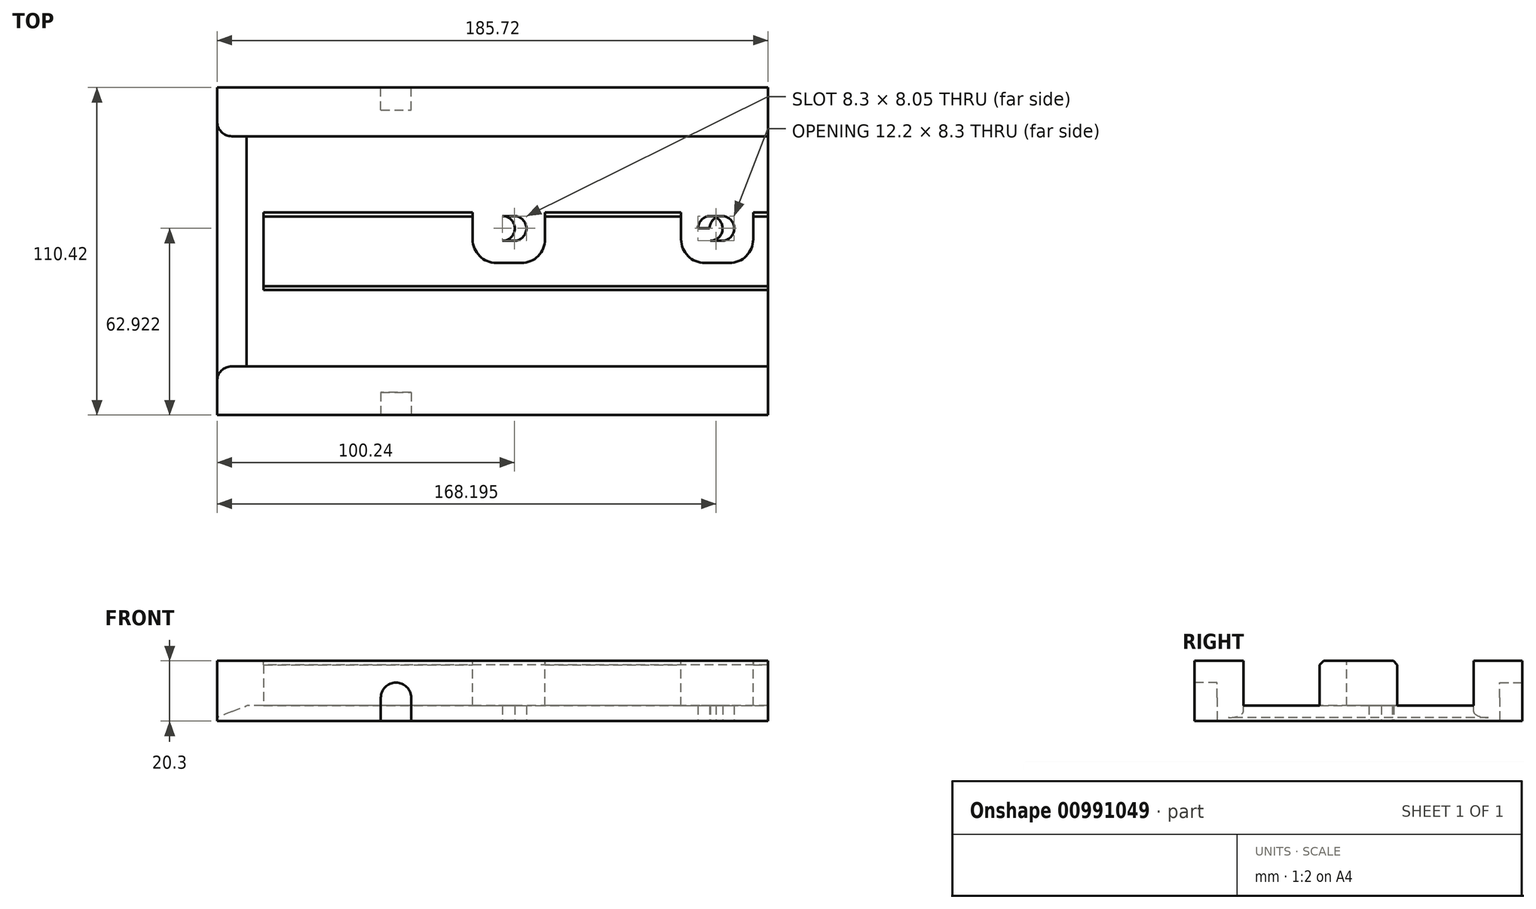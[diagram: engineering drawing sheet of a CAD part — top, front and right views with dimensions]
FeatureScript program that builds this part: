
annotation { "Feature Type Name" : "Feature", "Feature Type Description" : "" }
export const myFeature = defineFeature(function(context is Context, id is Id, definition is map)
    precondition{}
    {
        {
            var Q0;
            Q0=qCreatedBy(makeId("Top.planeOp"),FACE);
            var sketch = newSketch(context, id + "F0", { "sketchPlane" : qUnion([Q0])});
            skLineSegment(sketch, "E0.bottom", {"start": v(-101.07, 45.3) * mm, "end": v(84.65, 45.3) * mm});
            skLineSegment(sketch, "E0.top", {"start": v(-101.07, -65.12) * mm, "end": v(84.65, -65.12) * mm});
            skLineSegment(sketch, "E0.left", {"start": v(-101.07, 45.3) * mm, "end": v(-101.07, -65.12) * mm});
            skLineSegment(sketch, "E0.right", {"start": v(84.65, 45.3) * mm, "end": v(84.65, -65.12) * mm});
            skSolve(sketch);
        }
        {
            var Q0;
            Q0 = qSketchRegion(id + "F0", true);
            extrude(context, id + "F1", {"entities" : qUnion([Q0]), "depth" : 5.2 * mm, "offsetDistance" : 25 * mm});
        }
        {
            var Q0;
            Q0=makeQuery(id+"F1.opExtrude","SWEPT_FACE",FACE,{"disambiguationData":[OSD([sQuery(id+"F0.wireOp",EDGE,"E0.top")])]});
            var sketch = newSketch(context, id + "F2", { "sketchPlane" : qUnion([Q0])});
            skLineSegment(sketch, "E1", {"start": v(-101.07, 5.2) * mm, "end": v(-91.07, 5.2) * mm});
            skLineSegment(sketch, "E2", {"start": v(-101.07, 1.2) * mm, "end": v(-91.07, 5.2) * mm});
            skLineSegment(sketch, "E3", {"start": v(-101.07, 1.2) * mm, "end": v(-101.07, 5.2) * mm});
            skLineSegment(sketch, "E4", {"start": v(-91.07, 5.2) * mm, "end": v(-101.07, 1.2) * mm});
            skSolve(sketch);
        }
        {
            var Q0;
            Q0=makeQuery(id+"F2.imprint","IMPRINT",FACE,{"disambiguationData":[TD([[makeQuery(id+"F2.imprint","IMPRINT",EDGE,{"derivedFrom":sQuery(id+"F2.wireOp",EDGE,"E1")}),-1.0]])]});
            extrude(context, id + "F3", {"entities" : qUnion([Q0]), "operationType" : NewBodyOperationType.REMOVE, "endBound" : BoundingType.UP_TO_NEXT, "oppositeDirection" : true, "depth" : 25 * mm, "offsetDistance" : 25 * mm});
        }
        {
            var Q0;
            Q0=makeQuery(id+"F1.opExtrude","CAP_FACE",FACE,{"disambiguationData":[OSD([sQuery(id+"F0.wireOp",EDGE,"E0.bottom"),sQuery(id+"F0.wireOp",EDGE,"E0.top"),sQuery(id+"F0.wireOp",EDGE,"E0.left"),sQuery(id+"F0.wireOp",EDGE,"E0.right")])],"isStart":true});
            var sketch = newSketch(context, id + "F4", { "sketchPlane" : qUnion([Q0])});
            skLineSegment(sketch, "E5.bottom", {"start": v(-101.07, 65.12) * mm, "end": v(84.65, 65.12) * mm});
            skLineSegment(sketch, "E5.top", {"start": v(-101.07, 48.72) * mm, "end": v(84.65, 48.72) * mm});
            skLineSegment(sketch, "E5.left", {"start": v(-101.07, 65.12) * mm, "end": v(-101.07, 48.72) * mm});
            skLineSegment(sketch, "E5.right", {"start": v(84.65, 65.12) * mm, "end": v(84.65, 48.72) * mm});
            skLineSegment(sketch, "E6.bottom", {"start": v(-101.07, -45.3) * mm, "end": v(84.65, -45.3) * mm});
            skLineSegment(sketch, "E6.top", {"start": v(-101.07, -28.9) * mm, "end": v(84.65, -28.9) * mm});
            skLineSegment(sketch, "E6.left", {"start": v(-101.07, -45.3) * mm, "end": v(-101.07, -28.9) * mm});
            skLineSegment(sketch, "E6.right", {"start": v(84.65, -45.3) * mm, "end": v(84.65, -28.9) * mm});
            skLineSegment(sketch, "E7.top", {"start": v(84.65, 22.96) * mm, "end": v(-85.35, 22.96) * mm});
            skLineSegment(sketch, "E7.left", {"start": v(84.65, 9.9) * mm, "end": v(84.65, 22.96) * mm});
            skLineSegment(sketch, "E7.right", {"start": v(-85.35, 9.9) * mm, "end": v(-85.35, 22.96) * mm});
            skLineSegment(sketch, "E8.top", {"start": v(-85.35, -3.14) * mm, "end": v(84.65, -3.14) * mm});
            skLineSegment(sketch, "E8.left", {"start": v(-85.35, 9.9) * mm, "end": v(-85.35, -3.14) * mm});
            skLineSegment(sketch, "E8.right", {"start": v(84.65, 9.9) * mm, "end": v(84.65, -3.14) * mm});
            skPoint(sketch, "E9.start.orphan", {"position": v(-101.07, 9.9) * mm});
            skSolve(sketch);
        }
        {
            var Q0;
            Q0 = qSketchRegion(id + "F4", true);
            extrude(context, id + "F5", {"entities" : qUnion([Q0]), "operationType" : NewBodyOperationType.ADD, "oppositeDirection" : true, "depth" : 20.3 * mm, "offsetDistance" : 25 * mm});
        }
        {
            var Q0;
            Q0=makeQuery(id+"F5.opExtrude","CAP_FACE",FACE,{"disambiguationData":[OSD([sQuery(id+"F4.wireOp",EDGE,"E7.top"),sQuery(id+"F4.wireOp",EDGE,"E7.left"),sQuery(id+"F4.wireOp",EDGE,"E7.right"),sQuery(id+"F4.wireOp",EDGE,"E8.top"),sQuery(id+"F4.wireOp",EDGE,"E8.left"),sQuery(id+"F4.wireOp",EDGE,"E8.right")])],"isStart":false});
            var sketch = newSketch(context, id + "F6", { "sketchPlane" : qUnion([Q0])});
            skLineSegment(sketch, "E10", {"start": v(84.65, 3.14) * mm, "end": v(79.65, 3.14) * mm});
            skLineSegment(sketch, "E11.bottom", {"start": v(79.65, 3.14) * mm, "end": v(55.35, 3.14) * mm});
            skLineSegment(sketch, "E11.top", {"start": v(79.65, -13.86) * mm, "end": v(55.35, -13.86) * mm});
            skLineSegment(sketch, "E11.left", {"start": v(79.65, 3.14) * mm, "end": v(79.65, -13.86) * mm});
            skLineSegment(sketch, "E11.right", {"start": v(55.35, 3.14) * mm, "end": v(55.35, -13.86) * mm});
            skLineSegment(sketch, "E12", {"start": v(84.65, 3.14) * mm, "end": v(9.49, 3.14) * mm});
            skLineSegment(sketch, "E13.bottom", {"start": v(9.49, 3.14) * mm, "end": v(-14.91, 3.14) * mm});
            skLineSegment(sketch, "E13.top", {"start": v(9.49, -13.86) * mm, "end": v(-14.91, -13.86) * mm});
            skLineSegment(sketch, "E13.left", {"start": v(9.49, 3.14) * mm, "end": v(9.49, -13.86) * mm});
            skLineSegment(sketch, "E13.right", {"start": v(-14.91, 3.14) * mm, "end": v(-14.91, -13.86) * mm});
            skSolve(sketch);
        }
        {
            var Q0;
            Q0=makeQuery(id+"F6.imprint","IMPRINT",FACE,{"disambiguationData":[TD([[makeQuery(id+"F6.imprint","IMPRINT",EDGE,{"derivedFrom":sQuery(id+"F6.wireOp",EDGE,"E13.bottom")}),-1.0]])]});
            var Q1;
            Q1=makeQuery(id+"F6.imprint","IMPRINT",FACE,{"disambiguationData":[TD([[makeQuery(id+"F6.imprint","IMPRINT",EDGE,{"derivedFrom":sQuery(id+"F6.wireOp",EDGE,"E11.bottom")}),-1.0]])]});
            extrude(context, id + "F7", {"entities" : qUnion([Q0, Q1]), "operationType" : NewBodyOperationType.REMOVE, "oppositeDirection" : true, "depth" : 15.1 * mm, "offsetDistance" : 25 * mm});
        }
        {
            var Q0;
            Q0=makeQuery(id+"F7.boolean.opBoolean","COPY",EDGE,{"derivedFrom":makeQuery(id+"F7.opExtrude","SWEPT_EDGE",EDGE,{"disambiguationData":[OSD([sQuery(id+"F6.wireOp",EDGE,"E13.top"),sQuery(id+"F6.wireOp",EDGE,"E13.right")])]})});
            fillet(context, id + "F8", {"entities" : qUnion([Q0]), "radius" : 8 * mm, "tangentPropagation" : true, "allowEdgeOverflow" : false});
        }
        {
            var Q0;
            Q0=makeQuery(id+"F7.boolean.opBoolean","COPY",EDGE,{"derivedFrom":makeQuery(id+"F7.opExtrude","SWEPT_EDGE",EDGE,{"disambiguationData":[OSD([sQuery(id+"F6.wireOp",EDGE,"E13.top"),sQuery(id+"F6.wireOp",EDGE,"E13.left")])]})});
            var Q1;
            Q1=makeQuery(id+"F7.boolean.opBoolean","COPY",EDGE,{"derivedFrom":makeQuery(id+"F7.opExtrude","SWEPT_EDGE",EDGE,{"disambiguationData":[OSD([sQuery(id+"F6.wireOp",EDGE,"E11.top"),sQuery(id+"F6.wireOp",EDGE,"E11.left")])]})});
            var Q2;
            Q2=makeQuery(id+"F7.boolean.opBoolean","COPY",EDGE,{"derivedFrom":makeQuery(id+"F7.opExtrude","SWEPT_EDGE",EDGE,{"disambiguationData":[OSD([sQuery(id+"F6.wireOp",EDGE,"E11.top"),sQuery(id+"F6.wireOp",EDGE,"E11.right")])]})});
            fillet(context, id + "F9", {"entities" : qUnion([Q0, Q1, Q2]), "radius" : 8 * mm, "tangentPropagation" : true, "allowEdgeOverflow" : false});
        }
        {
            var Q0;
            Q0=makeQuery(id+"F5.opExtrude","SWEPT_EDGE",EDGE,{"disambiguationData":[OSD([sQuery(id+"F0.wireOp",EDGE,"E0.left"),sQuery(id+"F4.wireOp",EDGE,"E6.top"),sQuery(id+"F4.wireOp",EDGE,"E6.left")])]});
            var Q1;
            Q1=makeQuery(id+"F5.opExtrude","SWEPT_EDGE",EDGE,{"disambiguationData":[OSD([sQuery(id+"F0.wireOp",EDGE,"E0.left"),sQuery(id+"F4.wireOp",EDGE,"E5.top"),sQuery(id+"F4.wireOp",EDGE,"E5.left")])]});
            fillet(context, id + "F10", {"entities" : qUnion([Q0, Q1]), "radius" : 5 * mm, "tangentPropagation" : true, "allowEdgeOverflow" : false});
        }
        {
            var Q0;
            {var subQ1=sQuery(id+"F4.wireOp",EDGE,"E8.top");Q0=makeQuery(id+"F7.boolean.opBoolean","SPLIT",EDGE,{"disambiguationData":[TD([makeQuery(id+"F7.opExtrude","SWEPT_FACE",FACE,{"disambiguationData":[OSD([sQuery(id+"F6.wireOp",EDGE,"E13.right")])]})])],"derivedFrom":makeQuery(id+"F5.opExtrude","CAP_EDGE",EDGE,{"disambiguationData":[OSD([subQ1])],"isStart":false})});}
            var Q1;
            {var subQ0=sQuery(id+"F4.wireOp",EDGE,"E8.top");Q1=makeQuery(id+"F7.boolean.opBoolean","SPLIT",EDGE,{"disambiguationData":[TD([makeQuery(id+"F7.opExtrude","SWEPT_FACE",FACE,{"disambiguationData":[OSD([sQuery(id+"F6.wireOp",EDGE,"E11.right")])]})])],"derivedFrom":makeQuery(id+"F5.opExtrude","CAP_EDGE",EDGE,{"disambiguationData":[OSD([subQ0])],"isStart":false})});}
            var Q2;
            {var subQ1=sQuery(id+"F4.wireOp",EDGE,"E8.top");Q2=makeQuery(id+"F7.boolean.opBoolean","SPLIT",EDGE,{"disambiguationData":[TD([makeQuery(id+"F1.opExtrude","SWEPT_FACE",FACE,{"disambiguationData":[OSD([sQuery(id+"F0.wireOp",EDGE,"E0.right")])]})])],"derivedFrom":makeQuery(id+"F5.opExtrude","CAP_EDGE",EDGE,{"disambiguationData":[OSD([subQ1])],"isStart":false})});}
            var Q3;
            Q3=makeQuery(id+"F5.opExtrude","CAP_EDGE",EDGE,{"disambiguationData":[OSD([sQuery(id+"F4.wireOp",EDGE,"E7.top")])],"isStart":false});
            chamfer(context, id + "F11", {"entities" : qUnion([Q0, Q1, Q2, Q3]), "width" : 1.3 * mm, "tangentPropagation" : true});
        }
        {
            var Q0;
            Q0=makeQuery(id+"F1.opExtrude","CAP_FACE",FACE,{"disambiguationData":[OSD([sQuery(id+"F0.wireOp",EDGE,"E0.bottom"),sQuery(id+"F0.wireOp",EDGE,"E0.top"),sQuery(id+"F0.wireOp",EDGE,"E0.left"),sQuery(id+"F0.wireOp",EDGE,"E0.right")])],"isStart":true});
            var sketch = newSketch(context, id + "F12", { "sketchPlane" : qUnion([Q0])});
            skLineSegment(sketch, "E14", {"start": v(-101.07, 65.12) * mm, "end": v(-101.07, -45.3) * mm});
            skLineSegment(sketch, "E15", {"start": v(84.65, -45.3) * mm, "end": v(84.65, 2.2) * mm});
            skLineSegment(sketch, "E16", {"start": v(84.65, 2.2) * mm, "end": v(69.08, 2.2) * mm});
            skCircle(sketch, "E17", {"center": v(69.08, 2.2) * mm, "radius": 4.15 * mm});
            skLineSegment(sketch, "E18", {"start": v(69.08, 2.2) * mm, "end": v(65.18, 2.2) * mm});
            skCircle(sketch, "E19", {"center": v(65.18, 2.2) * mm, "radius": 4.15 * mm});
            skLineSegment(sketch, "E20", {"start": v(65.18, 6.35) * mm, "end": v(69.08, 6.35) * mm});
            skLineSegment(sketch, "E21", {"start": v(65.18, -1.95) * mm, "end": v(69.08, -1.95) * mm});
            skLineSegment(sketch, "E22", {"start": v(84.65, 2.2) * mm, "end": v(-0.95, 2.2) * mm});
            skLineSegment(sketch, "E23", {"start": v(-0.95, 2.2) * mm, "end": v(-4.85, 2.2) * mm});
            skCircle(sketch, "E24", {"center": v(-0.95, 2.2) * mm, "radius": 4.15 * mm});
            skCircle(sketch, "E25", {"center": v(-4.85, 2.2) * mm, "radius": 4.15 * mm});
            skLineSegment(sketch, "E26", {"start": v(-4.85, 6.35) * mm, "end": v(-0.95, 6.35) * mm});
            skLineSegment(sketch, "E27", {"start": v(-4.85, -1.95) * mm, "end": v(-0.95, -1.95) * mm});
            skPoint(sketch, "E28", {"position": v(3.2, 2.2) * mm});
            skSolve(sketch);
        }
        {
            var Q0;
            Q0=makeQuery(id+"F5.boolean.opBoolean","MERGE",FACE,{"derivedFrom":[makeQuery(id+"F1.opExtrude","SWEPT_FACE",FACE,{"disambiguationData":[OSD([sQuery(id+"F0.wireOp",EDGE,"E0.top")])]}),makeQuery(id+"F5.opExtrude","SWEPT_FACE",FACE,{"disambiguationData":[OSD([sQuery(id+"F4.wireOp",EDGE,"E5.bottom")])]})]});
            var sketch = newSketch(context, id + "F13", { "sketchPlane" : qUnion([Q0])});
            skLineSegment(sketch, "E29", {"start": v(-101.07, 0) * mm, "end": v(-40.77, 0) * mm});
            skLineSegment(sketch, "E30", {"start": v(-40.77, 0) * mm, "end": v(-40.77, 7.91) * mm});
            skCircle(sketch, "E31", {"center": v(-40.77, 7.91) * mm, "radius": 5.1 * mm});
            skLineSegment(sketch, "E32", {"start": v(-45.87, 7.91) * mm, "end": v(-35.67, 7.91) * mm});
            skLineSegment(sketch, "E33.top", {"start": v(-45.87, 0) * mm, "end": v(-35.67, 0) * mm});
            skLineSegment(sketch, "E33.left", {"start": v(-45.87, 7.91) * mm, "end": v(-45.87, 0) * mm});
            skLineSegment(sketch, "E33.right", {"start": v(-35.67, 7.91) * mm, "end": v(-35.67, 0) * mm});
            skSolve(sketch);
        }
        {
            var Q0;
            Q0 = qSketchRegion(id + "F13", true);
            extrude(context, id + "F14", {"entities" : qUnion([Q0]), "operationType" : NewBodyOperationType.REMOVE, "oppositeDirection" : true, "depth" : 7.6 * mm, "offsetDistance" : 25 * mm});
        }
        {
            var Q0;
            Q0=makeQuery(id+"F5.boolean.opBoolean","MERGE",FACE,{"derivedFrom":[makeQuery(id+"F1.opExtrude","SWEPT_FACE",FACE,{"disambiguationData":[OSD([sQuery(id+"F0.wireOp",EDGE,"E0.bottom")])]}),makeQuery(id+"F5.opExtrude","SWEPT_FACE",FACE,{"disambiguationData":[OSD([sQuery(id+"F4.wireOp",EDGE,"E6.bottom")])]})]});
            var sketch = newSketch(context, id + "F15", { "sketchPlane" : qUnion([Q0])});
            skLineSegment(sketch, "E34.bottom", {"start": v(101.07, 0) * mm, "end": v(40.77, 0) * mm});
            skLineSegment(sketch, "E34.top", {"start": v(101.07, 7.9) * mm, "end": v(40.77, 7.9) * mm});
            skLineSegment(sketch, "E34.left", {"start": v(101.07, 0) * mm, "end": v(101.07, 7.9) * mm});
            skLineSegment(sketch, "E34.right", {"start": v(40.77, 0) * mm, "end": v(40.77, 7.9) * mm});
            skCircle(sketch, "E35", {"center": v(40.77, 7.9) * mm, "radius": 5.1 * mm});
            skLineSegment(sketch, "E36", {"start": v(45.87, 7.9) * mm, "end": v(35.67, 7.9) * mm});
            skLineSegment(sketch, "E37.bottom", {"start": v(35.67, 7.9) * mm, "end": v(45.87, 7.9) * mm});
            skLineSegment(sketch, "E37.top", {"start": v(35.67, 0) * mm, "end": v(45.87, 0) * mm});
            skLineSegment(sketch, "E37.left", {"start": v(35.67, 7.9) * mm, "end": v(35.67, 0) * mm});
            skLineSegment(sketch, "E37.right", {"start": v(45.87, 7.9) * mm, "end": v(45.87, 0) * mm});
            skSolve(sketch);
        }
        {
            var Q0;
            {var subQ3=sQuery(id+"F15.wireOp",EDGE,"E37.right");Q0=makeQuery(id+"F15.imprint","IMPRINT",FACE,{"disambiguationData":[TD([[makeQuery(id+"F15.imprint","IMPRINT",EDGE,{"derivedFrom":subQ3}),-1.0]])]});}
            var Q1;
            {var subQ0=sQuery(id+"F15.wireOp",EDGE,"E37.top");Q1=makeQuery(id+"F15.imprint","IMPRINT",FACE,{"disambiguationData":[TD([[makeQuery(id+"F15.imprint","IMPRINT",EDGE,{"derivedFrom":subQ0}),-1.0]])]});}
            var Q2;
            {var subQ0=sQuery(id+"F15.wireOp",EDGE,"E36");Q2=makeQuery(id+"F15.imprint","IMPRINT",FACE,{"disambiguationData":[TD([[makeQuery(id+"F15.imprint","IMPRINT",EDGE,{"derivedFrom":subQ0}),1.0]])]});}
            var Q3;
            {var subQ0=sQuery(id+"F15.wireOp",EDGE,"E34.right");var subQ3=sQuery(id+"F15.wireOp",EDGE,"E35");var subQ5=makeQuery(id+"F15.imprint","INTERSECT",VERTEX,{"derivedFrom":[subQ0,subQ3]});Q3=makeQuery(id+"F15.imprint","IMPRINT",FACE,{"disambiguationData":[TD([[makeQuery(id+"F15.imprint","IMPRINT",EDGE,{"disambiguationData":[TD([[subQ5,-1.0]])],"derivedFrom":subQ0}),-1.0]])]});}
            var Q4;
            {var subQ0=sQuery(id+"F15.wireOp",EDGE,"E36");Q4=makeQuery(id+"F15.imprint","IMPRINT",FACE,{"disambiguationData":[TD([[makeQuery(id+"F15.imprint","IMPRINT",EDGE,{"derivedFrom":subQ0}),-1.0]])]});}
            extrude(context, id + "F16", {"entities" : qUnion([Q0, Q1, Q2, Q3, Q4]), "operationType" : NewBodyOperationType.REMOVE, "oppositeDirection" : true, "depth" : 7.6 * mm, "offsetDistance" : 25 * mm});
        }
        {
            var Q0;
            {var subQ0=sQuery(id+"F12.wireOp",EDGE,"E20");Q0=makeQuery(id+"F12.imprint","IMPRINT",FACE,{"disambiguationData":[TD([[makeQuery(id+"F12.imprint","IMPRINT",EDGE,{"derivedFrom":subQ0}),-1.0]])]});}
            var Q1;
            {var subQ0=sQuery(id+"F12.wireOp",EDGE,"E21");Q1=makeQuery(id+"F12.imprint","IMPRINT",FACE,{"disambiguationData":[TD([[makeQuery(id+"F12.imprint","IMPRINT",EDGE,{"derivedFrom":subQ0}),1.0]])]});}
            var Q2;
            {var subQ0=sQuery(id+"F12.wireOp",EDGE,"E26");Q2=makeQuery(id+"F12.imprint","IMPRINT",FACE,{"disambiguationData":[TD([[makeQuery(id+"F12.imprint","IMPRINT",EDGE,{"derivedFrom":subQ0}),-1.0]])]});}
            var Q3;
            {var subQ0=sQuery(id+"F12.wireOp",EDGE,"E27");Q3=makeQuery(id+"F12.imprint","IMPRINT",FACE,{"disambiguationData":[TD([[makeQuery(id+"F12.imprint","IMPRINT",EDGE,{"derivedFrom":subQ0}),1.0]])]});}
            var Q4;
            {var subQ0=sQuery(id+"F12.wireOp",EDGE,"E17");var subQ1=makeQuery(id+"F12.imprint","INTERSECT",VERTEX,{"derivedFrom":[subQ0,sQuery(id+"F12.wireOp",EDGE,"E20")]});Q4=makeQuery(id+"F12.imprint","IMPRINT",FACE,{"disambiguationData":[TD([[makeQuery(id+"F12.imprint","IMPRINT",EDGE,{"disambiguationData":[TD([[subQ1,1.0]])],"derivedFrom":subQ0}),1.0]])]});}
            var Q5;
            {var subQ0=sQuery(id+"F12.wireOp",EDGE,"E19");var subQ1=sQuery(id+"F12.wireOp",EDGE,"E17");var subQ2=makeQuery(id+"F12.imprint","INTERSECT",VERTEX,{"disambiguationData":[OD(0.0)],"derivedFrom":[subQ1,subQ0]});Q5=makeQuery(id+"F12.imprint","IMPRINT",FACE,{"disambiguationData":[TD([[makeQuery(id+"F12.imprint","IMPRINT",EDGE,{"disambiguationData":[TD([[subQ2,-1.0]])],"derivedFrom":subQ1}),-1.0]])]});}
            var Q6;
            {var subQ0=sQuery(id+"F12.wireOp",EDGE,"E22");var subQ1=sQuery(id+"F12.wireOp",EDGE,"E17");var subQ2=makeQuery(id+"F12.imprint","INTERSECT",VERTEX,{"disambiguationData":[OD(1.0)],"derivedFrom":[subQ1,subQ0]});Q6=makeQuery(id+"F12.imprint","IMPRINT",FACE,{"disambiguationData":[TD([[makeQuery(id+"F12.imprint","IMPRINT",EDGE,{"disambiguationData":[TD([[subQ2,-1.0]])],"derivedFrom":subQ1}),-1.0]])]});}
            var Q7;
            {var subQ0=sQuery(id+"F12.wireOp",EDGE,"E17");var subQ1=makeQuery(id+"F12.imprint","INTERSECT",VERTEX,{"derivedFrom":[subQ0,sQuery(id+"F12.wireOp",EDGE,"E21")]});Q7=makeQuery(id+"F12.imprint","IMPRINT",FACE,{"disambiguationData":[TD([[makeQuery(id+"F12.imprint","IMPRINT",EDGE,{"disambiguationData":[TD([[subQ1,1.0]])],"derivedFrom":subQ0}),1.0]])]});}
            var Q8;
            {var subQ0=sQuery(id+"F12.wireOp",EDGE,"E24");var subQ1=sQuery(id+"F12.wireOp",EDGE,"E22");var subQ2=makeQuery(id+"F12.imprint","INTERSECT",VERTEX,{"derivedFrom":[subQ1,subQ0]});Q8=makeQuery(id+"F12.imprint","IMPRINT",FACE,{"disambiguationData":[TD([[makeQuery(id+"F12.imprint","IMPRINT",EDGE,{"disambiguationData":[TD([[subQ2,-1.0]])],"derivedFrom":subQ1}),1.0]])]});}
            var Q9;
            {var subQ0=sQuery(id+"F12.wireOp",EDGE,"E25");var subQ1=sQuery(id+"F12.wireOp",EDGE,"E24");var subQ2=makeQuery(id+"F12.imprint","INTERSECT",VERTEX,{"disambiguationData":[OD(0.0)],"derivedFrom":[subQ1,subQ0]});Q9=makeQuery(id+"F12.imprint","IMPRINT",FACE,{"disambiguationData":[TD([[makeQuery(id+"F12.imprint","IMPRINT",EDGE,{"disambiguationData":[TD([[subQ2,-1.0]])],"derivedFrom":subQ1}),-1.0]])]});}
            var Q10;
            {var subQ0=sQuery(id+"F12.wireOp",EDGE,"E24");var subQ1=sQuery(id+"F12.wireOp",EDGE,"E22");var subQ2=makeQuery(id+"F12.imprint","INTERSECT",VERTEX,{"derivedFrom":[subQ1,subQ0]});Q10=makeQuery(id+"F12.imprint","IMPRINT",FACE,{"disambiguationData":[TD([[makeQuery(id+"F12.imprint","IMPRINT",EDGE,{"disambiguationData":[TD([[subQ2,-1.0]])],"derivedFrom":subQ1}),-1.0]])]});}
            var Q11;
            {var subQ0=sQuery(id+"F12.wireOp",EDGE,"E25");var subQ1=sQuery(id+"F12.wireOp",EDGE,"E24");var subQ2=makeQuery(id+"F12.imprint","INTERSECT",VERTEX,{"disambiguationData":[OD(0.0)],"derivedFrom":[subQ1,subQ0]});Q11=makeQuery(id+"F12.imprint","IMPRINT",FACE,{"disambiguationData":[TD([[makeQuery(id+"F12.imprint","IMPRINT",EDGE,{"disambiguationData":[TD([[subQ2,-1.0]])],"derivedFrom":subQ1}),1.0]])]});}
            var Q12;
            {var subQ0=sQuery(id+"F12.wireOp",EDGE,"E22");var subQ6=makeQuery(id+"F12.imprint","IMPRINT",VERTEX,{"derivedFrom":subQ0});Q12=makeQuery(id+"F12.imprint","IMPRINT",FACE,{"disambiguationData":[TD([[makeQuery(id+"F12.imprint","IMPRINT",EDGE,{"disambiguationData":[TD([[subQ6,1.0]])],"derivedFrom":subQ0}),1.0]])]});}
            var Q13;
            {var subQ3=sQuery(id+"F12.wireOp",EDGE,"E22");var subQ6=makeQuery(id+"F12.imprint","IMPRINT",VERTEX,{"derivedFrom":subQ3});Q13=makeQuery(id+"F12.imprint","IMPRINT",FACE,{"disambiguationData":[TD([[makeQuery(id+"F12.imprint","IMPRINT",EDGE,{"disambiguationData":[TD([[subQ6,1.0]])],"derivedFrom":subQ3}),-1.0]])]});}
            extrude(context, id + "F17", {"entities" : qUnion([Q0, Q1, Q2, Q3, Q4, Q5, Q6, Q7, Q8, Q9, Q10, Q11, Q12, Q13]), "operationType" : NewBodyOperationType.REMOVE, "endBound" : BoundingType.THROUGH_ALL, "oppositeDirection" : true, "depth" : 25 * mm, "offsetDistance" : 25 * mm});
        }
    });
